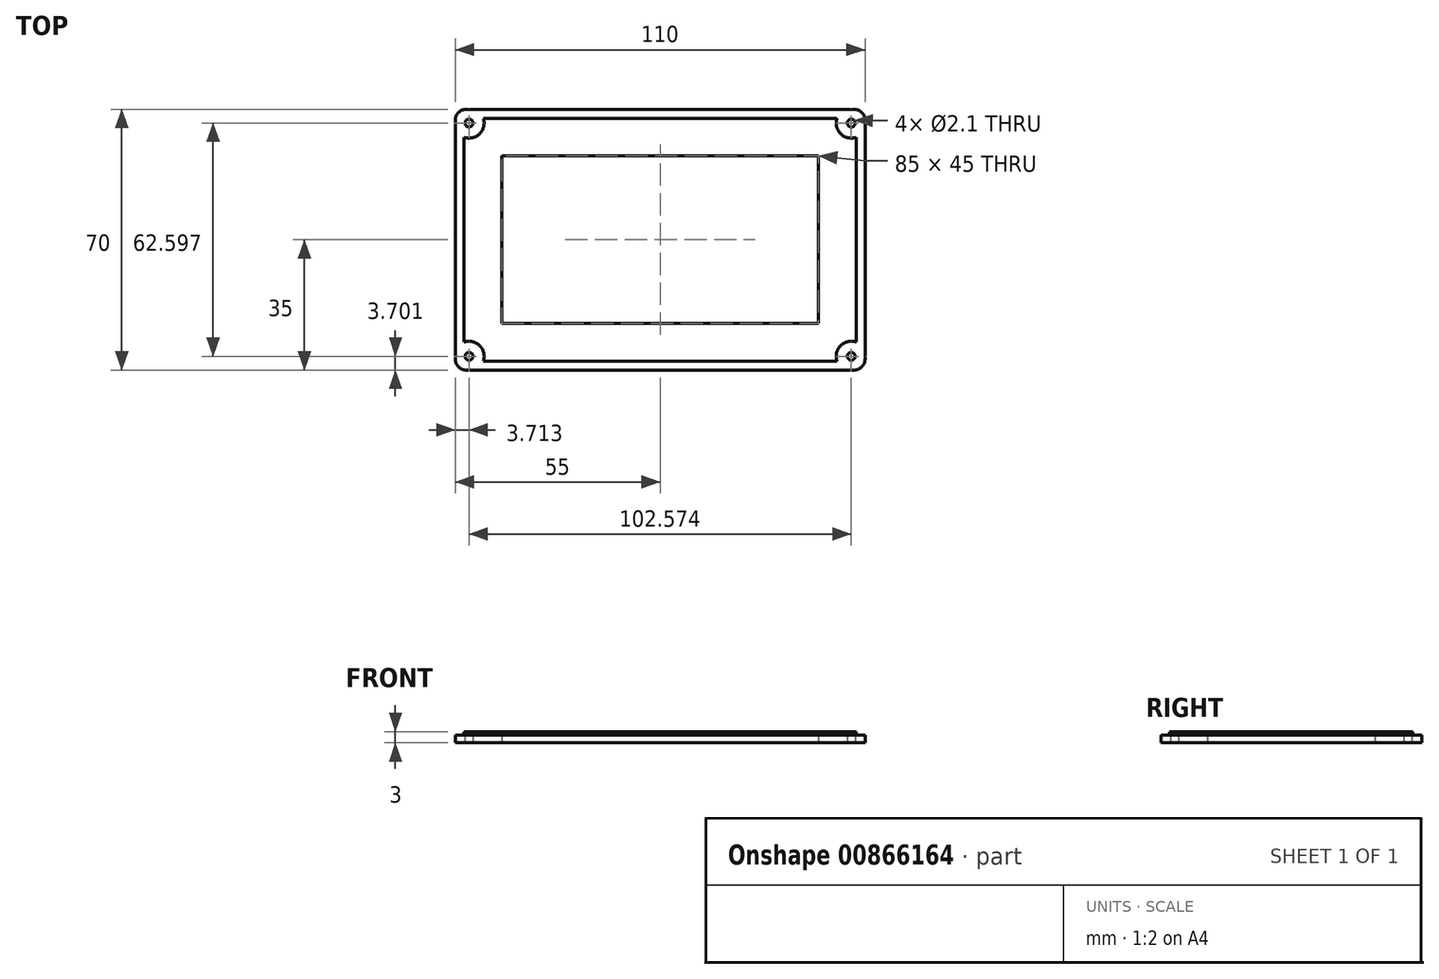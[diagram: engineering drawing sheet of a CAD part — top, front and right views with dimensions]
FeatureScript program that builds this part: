
annotation { "Feature Type Name" : "Feature", "Feature Type Description" : "" }
export const myFeature = defineFeature(function(context is Context, id is Id, definition is map)
    precondition{}
    {
        {
            var Q0;
            Q0=qCreatedBy(makeId("Top.planeOp"),FACE);
            var sketch = newSketch(context, id + "F0", { "sketchPlane" : qUnion([Q0])});
            skLineSegment(sketch, "E0.bottom", {"start": v(52, 35) * mm, "end": v(-52, 35) * mm});
            skLineSegment(sketch, "E0.top", {"start": v(52, -35) * mm, "end": v(-52, -35) * mm});
            skLineSegment(sketch, "E0.left", {"start": v(55, 32) * mm, "end": v(55, -32) * mm});
            skLineSegment(sketch, "E0.right", {"start": v(-55, 32) * mm, "end": v(-55, -32) * mm});
            skPoint(sketch, "E0.middle", {"position": v(0, 0) * mm});
            skPoint(sketch, "E1.visualSharp", {"position": v(-55, 35) * mm});
            skArc(sketch, "E1.filletArc", {"start": v(-52, 35) * mm, "mid": v(-54.12, 34.12) * mm, "end": v(-55, 32) * mm});
            skPoint(sketch, "E2.visualSharp", {"position": v(55, 35) * mm});
            skArc(sketch, "E2.filletArc", {"start": v(55, 32) * mm, "mid": v(54.12, 34.12) * mm, "end": v(52, 35) * mm});
            skPoint(sketch, "E3.visualSharp", {"position": v(-55, -35) * mm});
            skArc(sketch, "E3.filletArc", {"start": v(-55, -32) * mm, "mid": v(-54.12, -34.12) * mm, "end": v(-52, -35) * mm});
            skPoint(sketch, "E4.visualSharp", {"position": v(55, -35) * mm});
            skArc(sketch, "E4.filletArc", {"start": v(52, -35) * mm, "mid": v(54.12, -34.12) * mm, "end": v(55, -32) * mm});
            skPoint(sketch, "E5", {"position": v(-51.3, 31.3) * mm});
            skPoint(sketch, "E6.MirrorP", {"position": v(-51.3, -31.3) * mm});
            skPoint(sketch, "E7.MirrorP", {"position": v(51.3, -31.3) * mm});
            skPoint(sketch, "E8.MirrorP", {"position": v(51.3, 31.3) * mm});
            skCircle(sketch, "E9.0", {"center": v(-51.29, 31.3) * mm, "radius": 1.05 * mm});
            skCircle(sketch, "E10.MirrorC", {"center": v(-51.29, -31.3) * mm, "radius": 1.05 * mm});
            skCircle(sketch, "E11.MirrorC", {"center": v(51.29, 31.3) * mm, "radius": 1.05 * mm});
            skCircle(sketch, "E12.MirrorC", {"center": v(51.29, -31.3) * mm, "radius": 1.05 * mm});
            skLineSegment(sketch, "E13.bottom", {"start": v(42.5, 22.5) * mm, "end": v(-42.5, 22.5) * mm});
            skLineSegment(sketch, "E13.top", {"start": v(42.5, -22.5) * mm, "end": v(-42.5, -22.5) * mm});
            skLineSegment(sketch, "E13.left", {"start": v(42.5, 22.5) * mm, "end": v(42.5, -22.5) * mm});
            skLineSegment(sketch, "E13.right", {"start": v(-42.5, 22.5) * mm, "end": v(-42.5, -22.5) * mm});
            skArc(sketch, "E14.0", {"start": v(52.6, 27.47) * mm, "mid": v(48.43, 28.43) * mm, "end": v(47.45, 32.6) * mm});
            skLineSegment(sketch, "E14.1", {"start": v(52.6, 27.47) * mm, "end": v(52.6, -27.47) * mm});
            skLineSegment(sketch, "E14.2", {"start": v(47.45, 32.6) * mm, "end": v(-47.45, 32.6) * mm});
            skArc(sketch, "E14.3", {"start": v(52.6, -27.47) * mm, "mid": v(48.43, -28.43) * mm, "end": v(47.45, -32.6) * mm});
            skArc(sketch, "E14.4", {"start": v(-52.6, 27.47) * mm, "mid": v(-48.43, 28.43) * mm, "end": v(-47.45, 32.6) * mm});
            skLineSegment(sketch, "E14.5", {"start": v(-52.6, 27.47) * mm, "end": v(-52.6, -27.47) * mm});
            skArc(sketch, "E14.6", {"start": v(-52.6, -27.47) * mm, "mid": v(-48.43, -28.43) * mm, "end": v(-47.45, -32.6) * mm});
            skLineSegment(sketch, "E14.7", {"start": v(47.45, -32.6) * mm, "end": v(-47.45, -32.6) * mm});
            skSolve(sketch);
        }
        {
            var Q0;
            Q0=makeQuery(id+"F0.imprint","IMPRINT",FACE,{"disambiguationData":[TD([[makeQuery(id+"F0.imprint","IMPRINT",EDGE,{"derivedFrom":sQuery(id+"F0.wireOp",EDGE,"E0.bottom")}),1.0]])]});
            extrude(context, id + "F1", {"entities" : qUnion([Q0]), "depth" : 2 * mm, "offsetDistance" : 25 * mm});
        }
        {
            var Q0;
            Q0=makeQuery(id+"F0.imprint","IMPRINT",FACE,{"disambiguationData":[TD([[makeQuery(id+"F0.imprint","IMPRINT",EDGE,{"derivedFrom":sQuery(id+"F0.wireOp",EDGE,"E13.bottom")}),-1.0]])]});
            extrude(context, id + "F2", {"entities" : qUnion([Q0]), "operationType" : NewBodyOperationType.ADD, "depth" : 3 * mm, "offsetDistance" : 25 * mm});
        }
    });
